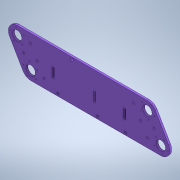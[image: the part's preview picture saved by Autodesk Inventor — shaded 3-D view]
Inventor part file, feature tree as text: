
AUTODESK INVENTOR PART (.ipt)
format: ipt  version: 2020 (Build 240168000, 168)  size: 305,152 bytes
history: native  units: mm
features: reference x26, other x4, extrude x2, sketch x2
ambient origin geometry x8: Origin, YZ Plane, XZ Plane, XY Plane, X Axis, Y Axis, Z Axis, Center Point
bodies: Body1 (feature_tree)
feature tree (34):
  extrude  "Выдавливание2"  Depth=40.0mm
  extrude  "Выдавливание3"  Depth=40.0mm
  sketch  "Эскиз1"
  sketch  "Эскиз2"
  reference  "Ссылка1"
  reference  "Ссылка2"
  reference  "Ссылка3"
  reference  "Ссылка4"
  reference  "Ссылка5"
  reference  "Ссылка6"
  reference  "Ссылка7"
  reference  "Ссылка8"
  reference  "Ссылка9"
  reference  "Ссылка10"
  reference  "Ссылка11"
  reference  "Ссылка12"
  reference  "Ссылка13"
  reference  "Ссылка14"
  reference  "Ссылка15"
  reference  "Ссылка17"
  reference  "Ссылка18"
  reference  "Ссылка19"
  reference  "Ссылка20"
  reference  "Ссылка21"
  reference  "Ссылка22"
  reference  "Ссылка23"
  reference  "Ссылка24"
  reference  "Ссылка25"
  reference  "Ссылка26"
  reference  "Ссылка27"
  parser-record x1  (decoder bookkeeping rows leaked as tree rows — omitted from the tree; the rows remain in map.json)
  other  "Сборка1.iam"
  other  "podsipnicoviy_ysel:1"
  other  "podsipnicoviy_ysel:2"
note: 1 file-system path scrubbed to <path> (originals preserved in map.json)
